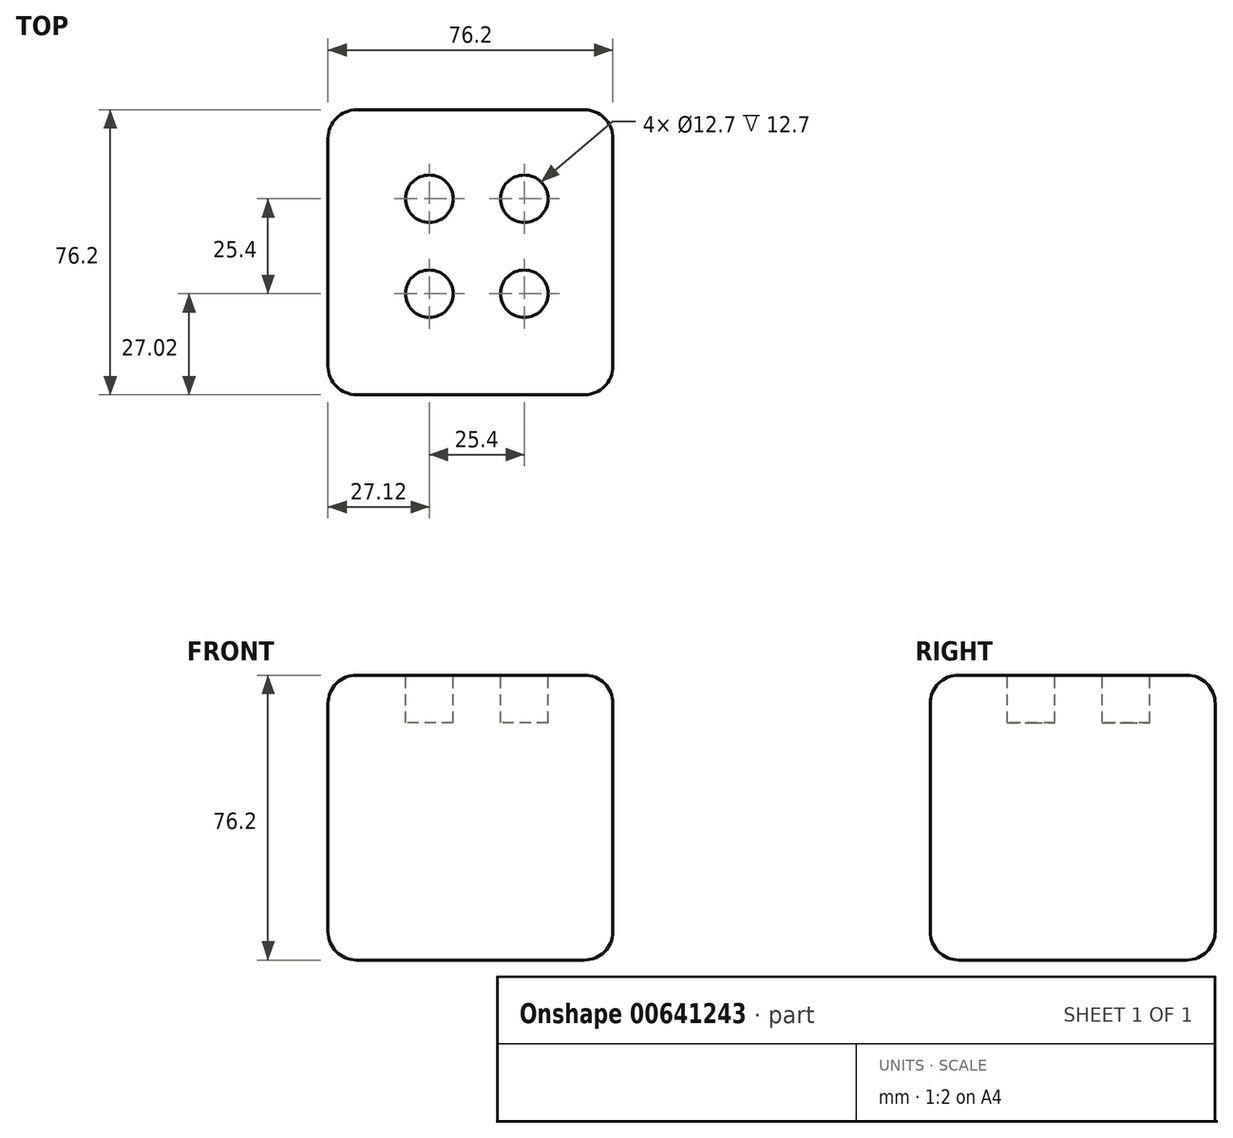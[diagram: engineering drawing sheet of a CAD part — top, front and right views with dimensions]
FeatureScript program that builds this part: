
annotation { "Feature Type Name" : "Feature", "Feature Type Description" : "" }
export const myFeature = defineFeature(function(context is Context, id is Id, definition is map)
    precondition{}
    {
        {
            var Q0;
            Q0=qCreatedBy(makeId("Top.planeOp"),FACE);
            var sketch = newSketch(context, id + "F0", { "sketchPlane" : qUnion([Q0])});
            skLineSegment(sketch, "E0.bottom", {"start": v(-39.82, -39.72) * mm, "end": v(36.38, -39.72) * mm});
            skLineSegment(sketch, "E0.top", {"start": v(-39.82, 36.48) * mm, "end": v(36.38, 36.48) * mm});
            skLineSegment(sketch, "E0.left", {"start": v(-39.82, -39.72) * mm, "end": v(-39.82, 36.48) * mm});
            skLineSegment(sketch, "E0.right", {"start": v(36.38, -39.72) * mm, "end": v(36.38, 36.48) * mm});
            skSolve(sketch);
        }
        {
            var Q0;
            Q0 = qSketchRegion(id + "F0", true);
            extrude(context, id + "F1", {"entities" : qUnion([Q0]), "depth" : 76.2 * mm, "offsetDistance" : 25.4 * mm});
        }
        {
            var Q0;
            Q0=makeQuery(id+"F1.opExtrude","CAP_EDGE",EDGE,{"disambiguationData":[OSD([sQuery(id+"F0.wireOp",EDGE,"E0.left")])],"isStart":false});
            var Q1;
            Q1=makeQuery(id+"F1.opExtrude","CAP_EDGE",EDGE,{"disambiguationData":[OSD([sQuery(id+"F0.wireOp",EDGE,"E0.bottom")])],"isStart":false});
            var Q2;
            Q2=makeQuery(id+"F1.opExtrude","SWEPT_EDGE",EDGE,{"disambiguationData":[OSD([sQuery(id+"F0.wireOp",EDGE,"E0.bottom"),sQuery(id+"F0.wireOp",EDGE,"E0.left")])]});
            var Q3;
            Q3=makeQuery(id+"F1.opExtrude","CAP_EDGE",EDGE,{"disambiguationData":[OSD([sQuery(id+"F0.wireOp",EDGE,"E0.left")])],"isStart":true});
            var Q4;
            Q4=makeQuery(id+"F1.opExtrude","CAP_EDGE",EDGE,{"disambiguationData":[OSD([sQuery(id+"F0.wireOp",EDGE,"E0.bottom")])],"isStart":true});
            var Q5;
            Q5=makeQuery(id+"F1.opExtrude","SWEPT_EDGE",EDGE,{"disambiguationData":[OSD([sQuery(id+"F0.wireOp",EDGE,"E0.bottom"),sQuery(id+"F0.wireOp",EDGE,"E0.right")])]});
            var Q6;
            Q6=makeQuery(id+"F1.opExtrude","SWEPT_EDGE",EDGE,{"disambiguationData":[OSD([sQuery(id+"F0.wireOp",EDGE,"E0.top"),sQuery(id+"F0.wireOp",EDGE,"E0.left")])]});
            var Q7;
            Q7=makeQuery(id+"F1.opExtrude","CAP_EDGE",EDGE,{"disambiguationData":[OSD([sQuery(id+"F0.wireOp",EDGE,"E0.top")])],"isStart":false});
            var Q8;
            Q8=makeQuery(id+"F1.opExtrude","CAP_EDGE",EDGE,{"disambiguationData":[OSD([sQuery(id+"F0.wireOp",EDGE,"E0.top")])],"isStart":true});
            var Q9;
            Q9=makeQuery(id+"F1.opExtrude","SWEPT_EDGE",EDGE,{"disambiguationData":[OSD([sQuery(id+"F0.wireOp",EDGE,"E0.top"),sQuery(id+"F0.wireOp",EDGE,"E0.right")])]});
            var Q10;
            Q10=makeQuery(id+"F1.opExtrude","CAP_EDGE",EDGE,{"disambiguationData":[OSD([sQuery(id+"F0.wireOp",EDGE,"E0.right")])],"isStart":true});
            var Q11;
            Q11=makeQuery(id+"F1.opExtrude","SWEPT_FACE",FACE,{"disambiguationData":[OSD([sQuery(id+"F0.wireOp",EDGE,"E0.right")])]});
            fillet(context, id + "F2", {"entities" : qUnion([Q0, Q1, Q2, Q3, Q4, Q5, Q6, Q7, Q8, Q9, Q10, Q11]), "radius" : 7.62 * mm, "tangentPropagation" : true, "allowEdgeOverflow" : false});
        }
        {
            var Q0;
            Q0=makeQuery(id+"F1.opExtrude","CAP_FACE",FACE,{"disambiguationData":[OSD([sQuery(id+"F0.wireOp",EDGE,"E0.bottom"),sQuery(id+"F0.wireOp",EDGE,"E0.top"),sQuery(id+"F0.wireOp",EDGE,"E0.left"),sQuery(id+"F0.wireOp",EDGE,"E0.right")])],"isStart":false});
            var sketch = newSketch(context, id + "F3", { "sketchPlane" : qUnion([Q0])});
            skCircle(sketch, "E1", {"center": v(-12.7, 12.7) * mm, "radius": 6.35 * mm});
            skCircle(sketch, "E2.0.1.0", {"center": v(-12.7, -12.7) * mm, "radius": 6.35 * mm});
            skCircle(sketch, "E2.1.0.0", {"center": v(12.7, 12.7) * mm, "radius": 6.35 * mm});
            skCircle(sketch, "E2.1.1.0", {"center": v(12.7, -12.7) * mm, "radius": 6.35 * mm});
            skLineSegment(sketch, "E2.direction1", {"start": v(-12.7, 12.7) * mm, "end": v(12.7, 12.7) * mm, "construction": true});
            skLineSegment(sketch, "E2.direction2", {"start": v(-12.7, 12.7) * mm, "end": v(-12.7, -12.7) * mm, "construction": true});
            skSolve(sketch);
        }
        {
            var Q0;
            Q0 = qSketchRegion(id + "F3", true);
            extrude(context, id + "F4", {"entities" : qUnion([Q0]), "operationType" : NewBodyOperationType.REMOVE, "oppositeDirection" : true, "depth" : 12.7 * mm, "offsetDistance" : 25.4 * mm});
        }
    });
